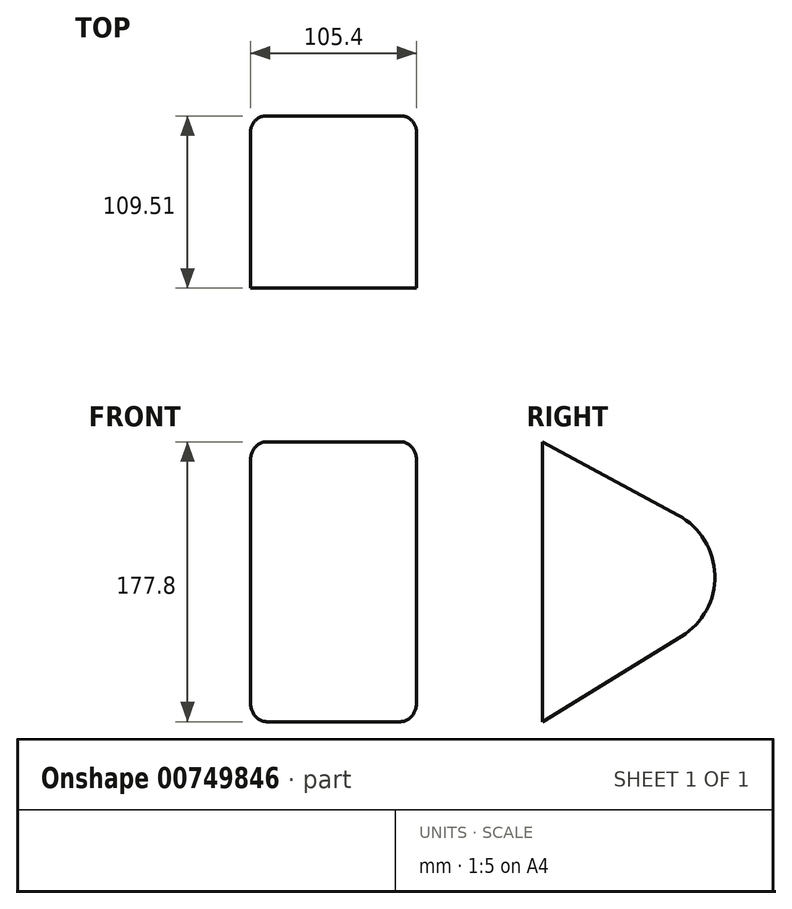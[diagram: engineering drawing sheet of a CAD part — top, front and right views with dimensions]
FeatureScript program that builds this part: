
annotation { "Feature Type Name" : "Feature", "Feature Type Description" : "" }
export const myFeature = defineFeature(function(context is Context, id is Id, definition is map)
    precondition{}
    {
        {
            var Q0;
            Q0=qCreatedBy(makeId("Right.planeOp"),FACE);
            var sketch = newSketch(context, id + "F0", { "sketchPlane" : qUnion([Q0])});
            skLineSegment(sketch, "E0.left", {"start": v(-73.9, 83.5) * mm, "end": v(-73.9, -94.3) * mm});
            skLineSegment(sketch, "E1", {"start": v(-73.9, 83.5) * mm, "end": v(80.1, 0) * mm});
            skLineSegment(sketch, "E2", {"start": v(80.1, 0) * mm, "end": v(-73.9, -94.3) * mm});
            skSolve(sketch);
        }
        {
            var Q0;
            Q0 = qSketchRegion(id + "F0", true);
            extrude(context, id + "F1", {"entities" : qUnion([Q0]), "endBound" : BoundingType.SYMMETRIC, "depth" : 105.4 * mm, "offsetDistance" : 25.4 * mm});
        }
        {
            var Q0;
            Q0=makeQuery(id+"F1.opExtrude","CAP_EDGE",EDGE,{"disambiguationData":[OSD([sQuery(id+"F0.wireOp",EDGE,"E1")])],"isStart":true});
            var Q1;
            Q1=makeQuery(id+"F1.opExtrude","CAP_EDGE",EDGE,{"disambiguationData":[OSD([sQuery(id+"F0.wireOp",EDGE,"E1")])],"isStart":false});
            var Q2;
            Q2=makeQuery(id+"F1.opExtrude","CAP_EDGE",EDGE,{"disambiguationData":[OSD([sQuery(id+"F0.wireOp",EDGE,"E2")])],"isStart":false});
            var Q3;
            Q3=makeQuery(id+"F1.opExtrude","CAP_EDGE",EDGE,{"disambiguationData":[OSD([sQuery(id+"F0.wireOp",EDGE,"E2")])],"isStart":true});
            fillet(context, id + "F2", {"entities" : qUnion([Q0, Q1, Q2, Q3]), "radius" : 10.16 * mm, "tangentPropagation" : true, "allowEdgeOverflow" : false});
        }
        {
            var Q0;
            Q0=makeQuery(id+"F1.opExtrude","SWEPT_EDGE",EDGE,{"disambiguationData":[OSD([sQuery(id+"F0.wireOp",EDGE,"E1"),sQuery(id+"F0.wireOp",EDGE,"E2")])]});
            fillet(context, id + "F3", {"entities" : qUnion([Q0]), "radius" : 44.45 * mm, "tangentPropagation" : true, "allowEdgeOverflow" : false});
        }
    });
